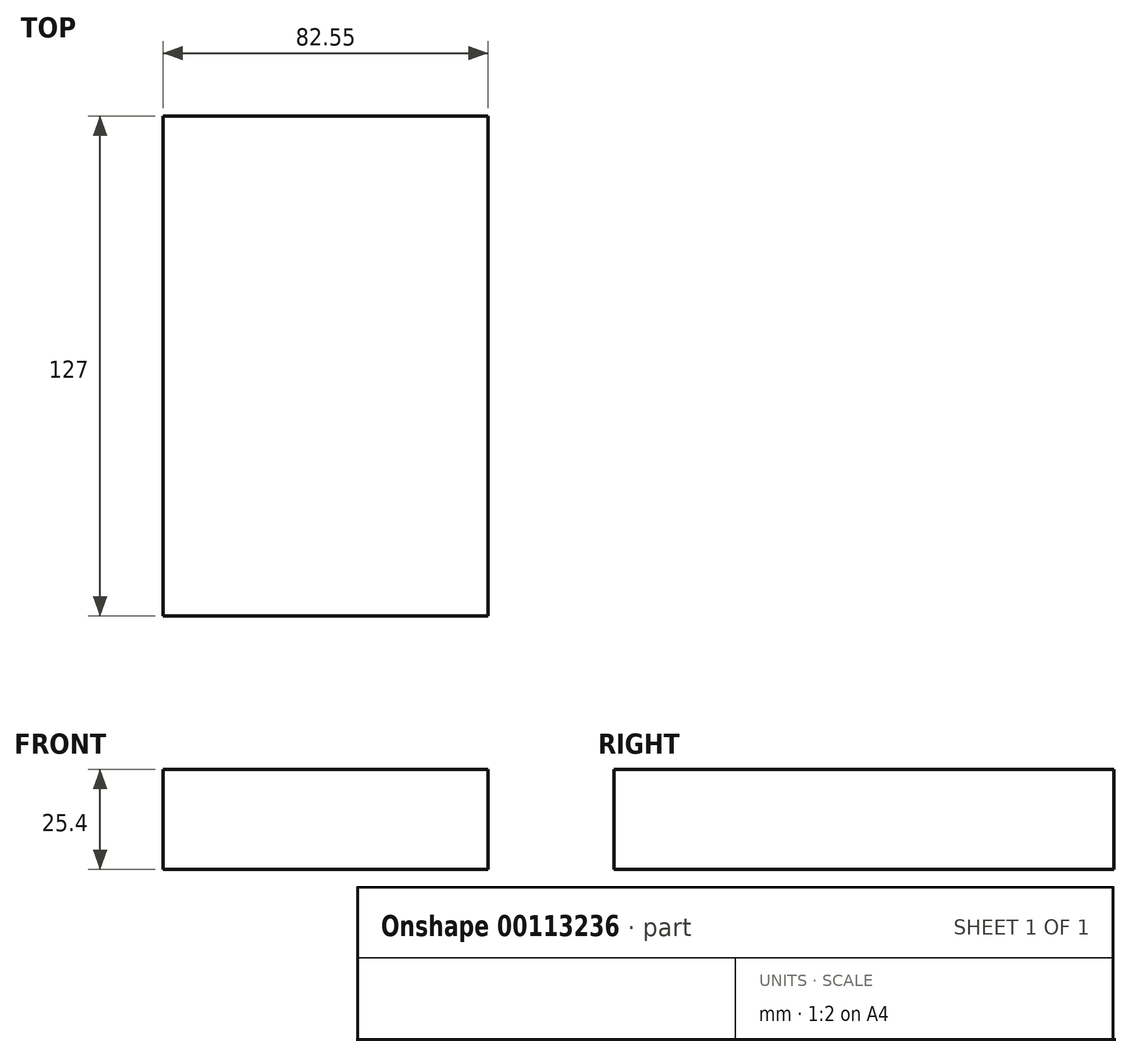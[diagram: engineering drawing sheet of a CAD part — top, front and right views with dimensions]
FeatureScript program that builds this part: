
annotation { "Feature Type Name" : "Feature", "Feature Type Description" : "" }
export const myFeature = defineFeature(function(context is Context, id is Id, definition is map)
    precondition{}
    {
        {
            var Q0;
            Q0=qCreatedBy(makeId("Front.planeOp"),FACE);
            var sketch = newSketch(context, id + "F0", { "sketchPlane" : qUnion([Q0])});
            skLineSegment(sketch, "E0.bottom", {"start": v(41.28, -12.7) * mm, "end": v(-41.28, -12.7) * mm});
            skLineSegment(sketch, "E0.top", {"start": v(41.28, 12.7) * mm, "end": v(-41.28, 12.7) * mm});
            skLineSegment(sketch, "E0.left", {"start": v(41.28, -12.7) * mm, "end": v(41.28, 12.7) * mm});
            skLineSegment(sketch, "E0.right", {"start": v(-41.27, -12.7) * mm, "end": v(-41.28, 12.7) * mm});
            skPoint(sketch, "E0.middle", {"position": v(0, 0) * mm});
            skLineSegment(sketch, "E1.bottom", {"start": v(109.57, 34.93) * mm, "end": v(58.77, 34.93) * mm});
            skLineSegment(sketch, "E1.top", {"start": v(109.57, 63.5) * mm, "end": v(58.77, 63.5) * mm});
            skLineSegment(sketch, "E1.left", {"start": v(109.57, 34.93) * mm, "end": v(109.57, 63.5) * mm});
            skLineSegment(sketch, "E1.right", {"start": v(58.77, 34.92) * mm, "end": v(58.77, 63.5) * mm});
            skPoint(sketch, "E1.middle", {"position": v(84.17, 49.21) * mm});
            skLineSegment(sketch, "E2", {"start": v(41.27, 12.7) * mm, "end": v(41.27, 23.83) * mm});
            skArc(sketch, "E3", {"start": v(57.15, 39.7) * mm, "mid": v(45.92, 35.05) * mm, "end": v(41.27, 23.83) * mm});
            skLineSegment(sketch, "E4", {"start": v(57.15, 39.7) * mm, "end": v(84.17, 39.7) * mm});
            skLineSegment(sketch, "E5.0", {"start": v(57.15, 58.75) * mm, "end": v(84.17, 58.75) * mm});
            skArc(sketch, "E5.1", {"start": v(57.15, 58.75) * mm, "mid": v(32.45, 48.52) * mm, "end": v(22.22, 23.83) * mm});
            skLineSegment(sketch, "E5.2", {"start": v(22.22, 9.53) * mm, "end": v(22.22, 23.83) * mm});
            skLineSegment(sketch, "E6", {"start": v(84.17, 34.93) * mm, "end": v(84.17, 63.5) * mm});
            skFitSpline(sketch, "E7", {"points": [v(-41.28, 12.7) * mm, v(57.15, 58.75) * mm], "startDerivative": vector(0, 118.1) * mm, "endDerivative": vector(171.45, -7.12) * mm});
            skSolve(sketch);
        }
        {
            var Q0;
            Q0=makeQuery(id+"F0.imprint","IMPRINT",FACE,{"disambiguationData":[TD([[makeQuery(id+"F0.imprint","IMPRINT",EDGE,{"derivedFrom":sQuery(id+"F0.wireOp",EDGE,"E0.bottom")}),-1.0]])]});
            extrude(context, id + "F1", {"entities" : qUnion([Q0]), "endBound" : BoundingType.SYMMETRIC, "depth" : 127 * mm});
        }
    });
